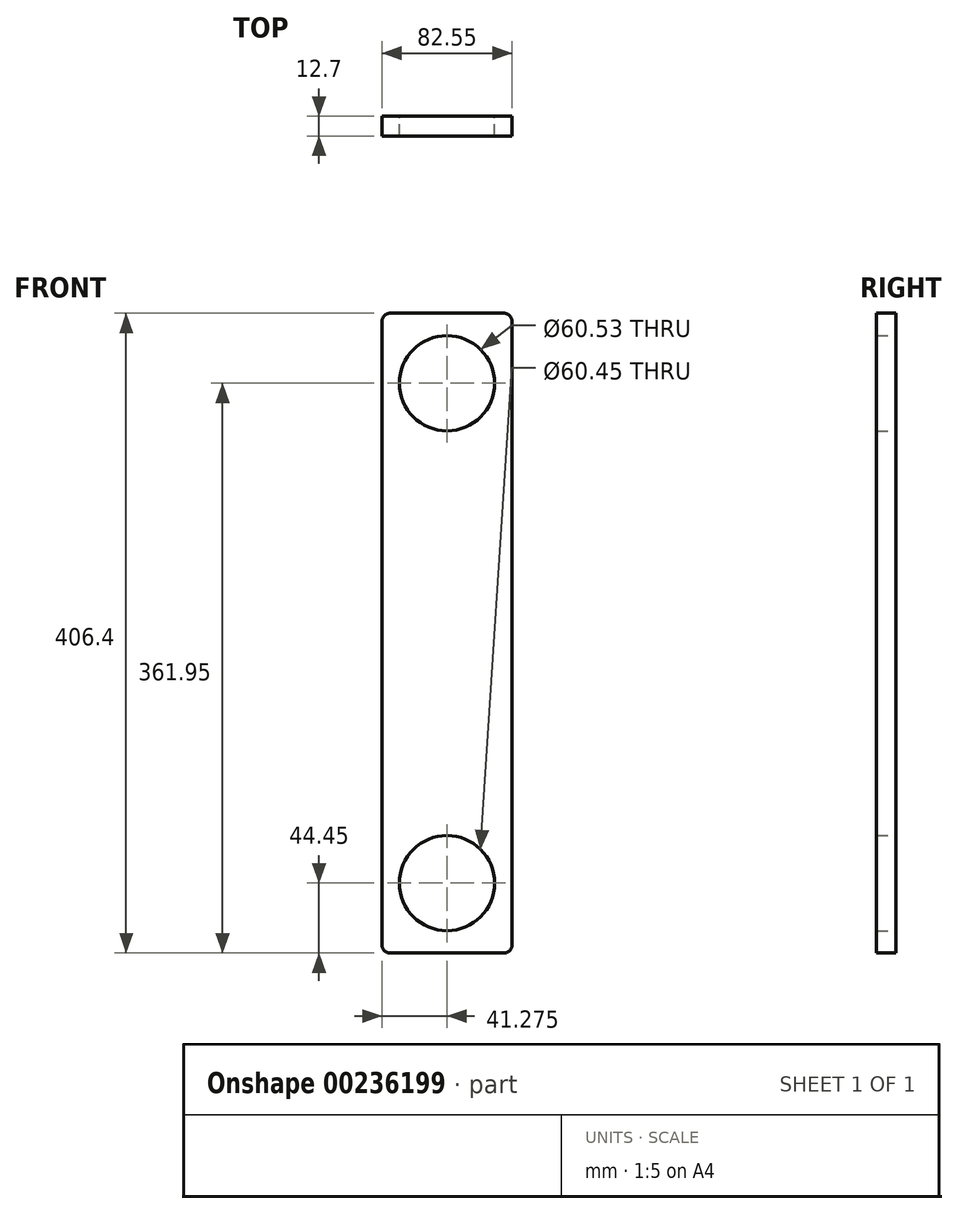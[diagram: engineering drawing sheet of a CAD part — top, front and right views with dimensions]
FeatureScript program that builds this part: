
annotation { "Feature Type Name" : "Feature", "Feature Type Description" : "" }
export const myFeature = defineFeature(function(context is Context, id is Id, definition is map)
    precondition{}
    {
        {
            var Q0;
            Q0=qCreatedBy(makeId("Front.planeOp"),FACE);
            var sketch = newSketch(context, id + "F0", { "sketchPlane" : qUnion([Q0])});
            skLineSegment(sketch, "E0", {"start": v(0, 0) * mm, "end": v(82.55, 0) * mm});
            skLineSegment(sketch, "E1", {"start": v(82.55, 0) * mm, "end": v(82.55, 406.4) * mm});
            skLineSegment(sketch, "E2", {"start": v(0, 0) * mm, "end": v(0, 406.4) * mm});
            skLineSegment(sketch, "E3", {"start": v(0, 406.4) * mm, "end": v(82.55, 406.4) * mm});
            skLineSegment(sketch, "E4", {"start": v(41.28, 406.4) * mm, "end": v(41.28, 361.95) * mm});
            skLineSegment(sketch, "E5", {"start": v(41.28, 0) * mm, "end": v(41.28, 44.45) * mm});
            skCircle(sketch, "E6", {"center": v(41.28, 44.45) * mm, "radius": 30.23 * mm});
            skCircle(sketch, "E7", {"center": v(41.28, 361.95) * mm, "radius": 30.26 * mm});
            skSolve(sketch);
        }
        {
            var Q0;
            Q0 = qSketchRegion(id + "F0", true);
            extrude(context, id + "F1", {"entities" : qUnion([Q0]), "depth" : 12.7 * mm});
        }
        {
            var Q0;
            Q0=makeQuery(id+"F1.opExtrude","SWEPT_EDGE",EDGE,{"disambiguationData":[OSD([sQuery(id+"F0.wireOp",EDGE,"E1"),sQuery(id+"F0.wireOp",EDGE,"E3")])]});
            fillet(context, id + "F2", {"entities" : qUnion([Q0]), "radius" : 5.08 * mm, "tangentPropagation" : true, "allowEdgeOverflow" : false});
        }
        {
            var Q0;
            Q0=makeQuery(id+"F1.opExtrude","SWEPT_EDGE",EDGE,{"disambiguationData":[OSD([sQuery(id+"F0.wireOp",EDGE,"E2"),sQuery(id+"F0.wireOp",EDGE,"E3")])]});
            var Q1;
            Q1=makeQuery(id+"F1.opExtrude","SWEPT_EDGE",EDGE,{"disambiguationData":[OSD([sQuery(id+"F0.wireOp",EDGE,"E0"),sQuery(id+"F0.wireOp",EDGE,"E1")])]});
            var Q2;
            Q2=makeQuery(id+"F1.opExtrude","SWEPT_EDGE",EDGE,{"disambiguationData":[OSD([sQuery(id+"F0.wireOp",EDGE,"E0"),sQuery(id+"F0.wireOp",EDGE,"E2")])]});
            fillet(context, id + "F3", {"entities" : qUnion([Q0, Q1, Q2]), "radius" : 5.08 * mm, "tangentPropagation" : true, "allowEdgeOverflow" : false});
        }
    });
